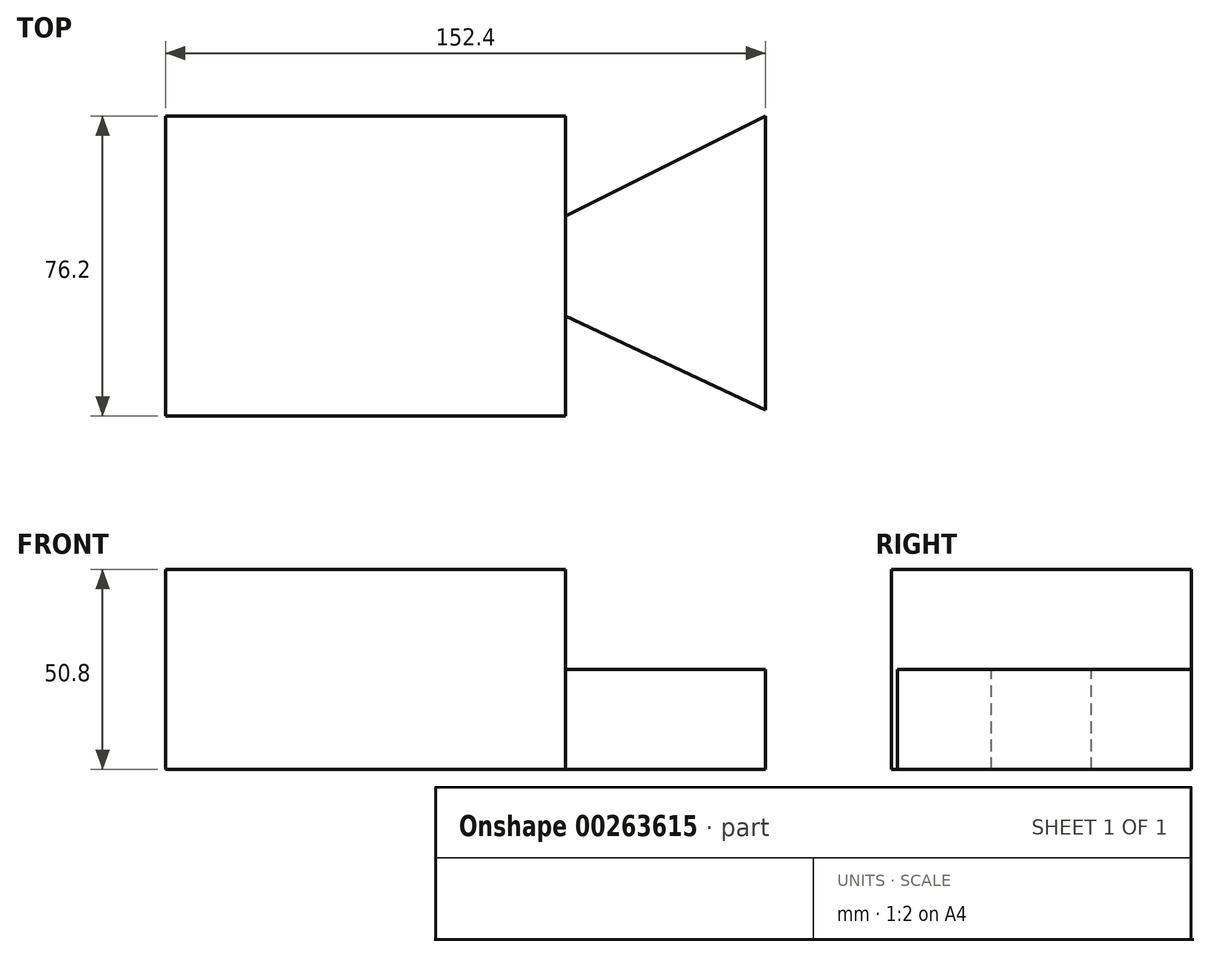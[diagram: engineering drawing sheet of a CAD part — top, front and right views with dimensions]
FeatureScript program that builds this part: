
annotation { "Feature Type Name" : "Feature", "Feature Type Description" : "" }
export const myFeature = defineFeature(function(context is Context, id is Id, definition is map)
    precondition{}
    {
        {
            var Q0;
            Q0=qCreatedBy(makeId("Front.planeOp"),FACE);
            var sketch = newSketch(context, id + "F0", { "sketchPlane" : qUnion([Q0])});
            skLineSegment(sketch, "E0", {"start": v(-75.79, 0) * mm, "end": v(25.81, 0) * mm});
            skLineSegment(sketch, "E1", {"start": v(25.81, 0) * mm, "end": v(25.81, 50.8) * mm});
            skLineSegment(sketch, "E2", {"start": v(25.81, 50.8) * mm, "end": v(-75.79, 50.8) * mm});
            skLineSegment(sketch, "E3", {"start": v(-75.79, 50.8) * mm, "end": v(-75.79, 0) * mm});
            skSolve(sketch);
        }
        {
            var Q0;
            Q0=makeQuery(id+"F0.imprint","IMPRINT",FACE,{"disambiguationData":[TD([[makeQuery(id+"F0.imprint","IMPRINT",EDGE,{"derivedFrom":sQuery(id+"F0.wireOp",EDGE,"E0")}),1.0]])]});
            extrude(context, id + "F1", {"entities" : qUnion([Q0]), "depth" : 76.2 * mm});
        }
        {
            var Q0;
            Q0=makeQuery(id+"F1.opExtrude","SWEPT_FACE",FACE,{"disambiguationData":[OSD([sQuery(id+"F0.wireOp",EDGE,"E1")])]});
            var sketch = newSketch(context, id + "F2", { "sketchPlane" : qUnion([Q0])});
            skLineSegment(sketch, "E4", {"start": v(-76.2, 0) * mm, "end": v(0, 0) * mm});
            skLineSegment(sketch, "E5", {"start": v(0, 0) * mm, "end": v(0, 25.4) * mm});
            skLineSegment(sketch, "E6", {"start": v(0, 25.4) * mm, "end": v(-76.2, 25.4) * mm});
            skLineSegment(sketch, "E7", {"start": v(-76.2, 25.4) * mm, "end": v(-76.2, 0) * mm});
            skSolve(sketch);
        }
        {
            var Q0;
            Q0=makeQuery(id+"F2.imprint","IMPRINT",FACE,{"disambiguationData":[TD([[makeQuery(id+"F2.imprint","IMPRINT",EDGE,{"derivedFrom":sQuery(id+"F2.wireOp",EDGE,"E4")}),1.0]])]});
            extrude(context, id + "F3", {"entities" : qUnion([Q0]), "operationType" : NewBodyOperationType.ADD, "depth" : 50.8 * mm});
        }
        {
            var Q0;
            Q0=makeQuery(id+"F3.opExtrude","SWEPT_FACE",FACE,{"disambiguationData":[OSD([sQuery(id+"F2.wireOp",EDGE,"E6")])]});
            var sketch = newSketch(context, id + "F4", { "sketchPlane" : qUnion([Q0])});
            skLineSegment(sketch, "E8", {"start": v(25.81, -76.2) * mm, "end": v(25.81, -50.8) * mm});
            skLineSegment(sketch, "E9", {"start": v(25.81, -50.8) * mm, "end": v(79.9, -76.2) * mm});
            skLineSegment(sketch, "E10", {"start": v(79.9, -76.2) * mm, "end": v(25.81, -76.2) * mm});
            skSolve(sketch);
        }
        {
            var Q0;
            {var subQ0=sQuery(id+"F4.wireOp",EDGE,"E8");Q0=makeQuery(id+"F4.imprint","IMPRINT",FACE,{"disambiguationData":[TD([[makeQuery(id+"F4.imprint","IMPRINT",EDGE,{"derivedFrom":subQ0}),1.0]])]});}
            extrude(context, id + "F5", {"entities" : qUnion([Q0]), "operationType" : NewBodyOperationType.REMOVE, "oppositeDirection" : true, "depth" : 25.4 * mm});
        }
        {
            var Q0;
            Q0=makeQuery(id+"F3.opExtrude","SWEPT_FACE",FACE,{"disambiguationData":[OSD([sQuery(id+"F2.wireOp",EDGE,"E6")])]});
            var sketch = newSketch(context, id + "F6", { "sketchPlane" : qUnion([Q0])});
            skLineSegment(sketch, "E11", {"start": v(25.81, -25.4) * mm, "end": v(76.61, 0) * mm});
            skLineSegment(sketch, "E12", {"start": v(76.61, 0) * mm, "end": v(25.81, 0) * mm});
            skLineSegment(sketch, "E13", {"start": v(25.81, 0) * mm, "end": v(25.81, -25.4) * mm});
            skSolve(sketch);
        }
        {
            var Q0;
            Q0=makeQuery(id+"F6.imprint","IMPRINT",FACE,{"disambiguationData":[TD([[makeQuery(id+"F6.imprint","IMPRINT",EDGE,{"derivedFrom":sQuery(id+"F6.wireOp",EDGE,"E11")}),1.0]])]});
            extrude(context, id + "F7", {"entities" : qUnion([Q0]), "operationType" : NewBodyOperationType.REMOVE, "oppositeDirection" : true, "depth" : 25.4 * mm});
        }
    });
